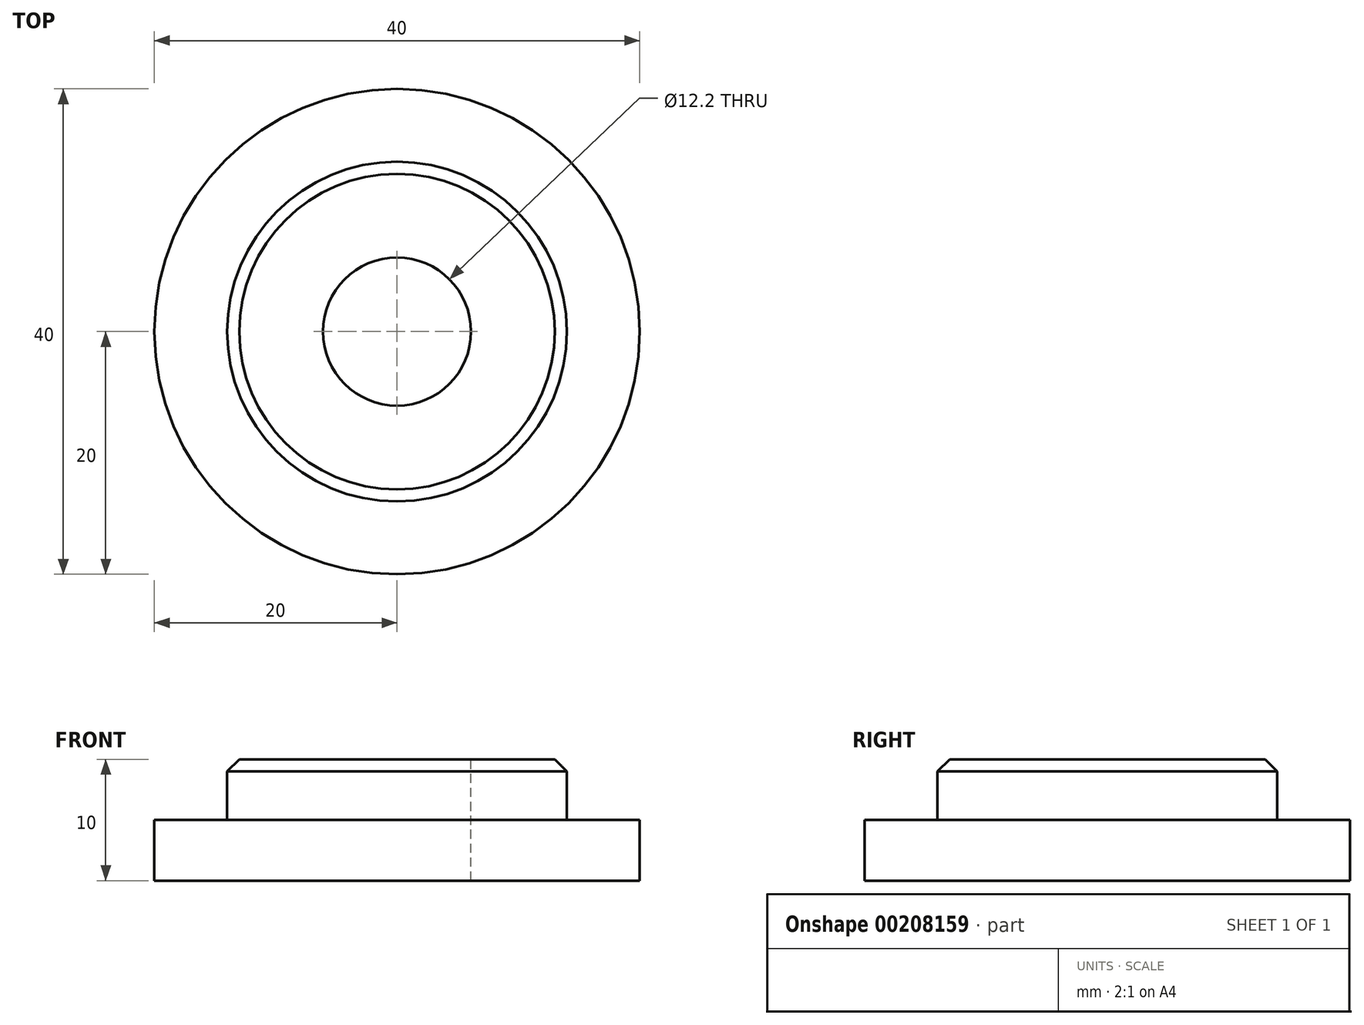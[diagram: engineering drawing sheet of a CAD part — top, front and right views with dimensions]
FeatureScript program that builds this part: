
annotation { "Feature Type Name" : "Feature", "Feature Type Description" : "" }
export const myFeature = defineFeature(function(context is Context, id is Id, definition is map)
    precondition{}
    {
        {
            var Q0;
            Q0=qCreatedBy(makeId("Top.planeOp"),FACE);
            var sketch = newSketch(context, id + "F0", { "sketchPlane" : qUnion([Q0])});
            skCircle(sketch, "E0", {"center": v(0, 0) * mm, "radius": 20 * mm});
            skSolve(sketch);
        }
        {
            var Q0;
            Q0=makeQuery(id+"F0.imprint","IMPRINT",FACE,{"disambiguationData":[TD([[makeQuery(id+"F0.imprint","IMPRINT",EDGE,{"derivedFrom":sQuery(id+"F0.wireOp",EDGE,"E0")}),1.0]])]});
            extrude(context, id + "F1", {"entities" : qUnion([Q0]), "depth" : 5 * mm});
        }
        {
            var Q0;
            Q0=makeQuery(id+"F1.opExtrude","CAP_FACE",FACE,{"disambiguationData":[OSD([sQuery(id+"F0.wireOp",EDGE,"E0")])],"isStart":false});
            var sketch = newSketch(context, id + "F2", { "sketchPlane" : qUnion([Q0])});
            skCircle(sketch, "E1", {"center": v(0, 0) * mm, "radius": 14 * mm});
            skSolve(sketch);
        }
        {
            var Q0;
            Q0=makeQuery(id+"F2.imprint","IMPRINT",FACE,{"disambiguationData":[TD([[makeQuery(id+"F2.imprint","IMPRINT",EDGE,{"derivedFrom":sQuery(id+"F2.wireOp",EDGE,"E1")}),1.0]])]});
            extrude(context, id + "F3", {"entities" : qUnion([Q0]), "operationType" : NewBodyOperationType.ADD, "depth" : 5 * mm});
        }
        {
            var Q0;
            Q0=makeQuery(id+"F1.opExtrude","CAP_FACE",FACE,{"disambiguationData":[OSD([sQuery(id+"F0.wireOp",EDGE,"E0")])],"isStart":true});
            var sketch = newSketch(context, id + "F4", { "sketchPlane" : qUnion([Q0])});
            skPoint(sketch, "E2", {"position": v(0, 0) * mm});
            skSolve(sketch);
        }
        {
            var Q0;
            Q0=sQuery(id+"F4.wireOp",VERTEX,"E2");
            var Q1;
            Q1=makeQuery(id+"F1.opExtrude","SWEPT_BODY",BODY,{"disambiguationData":[OSD([sQuery(id+"F0.wireOp",EDGE,"E0")])]});
            hole(context, id + "F5", {"style" : HoleStyle.SIMPLE, "endStyle" : HoleEndStyle.THROUGH, "holeDiameter" : 12.2 * mm, "locations" : qUnion([Q0]), "scope" : qUnion([Q1]), "isTappedThrough" : true, "startStyle" : HoleStartStyle.PART});
        }
        {
            var Q0;
            Q0=makeQuery(id+"F3.opExtrude","CAP_EDGE",EDGE,{"disambiguationData":[OSD([sQuery(id+"F2.wireOp",EDGE,"E1")])],"isStart":false});
            chamfer(context, id + "F6", {"entities" : qUnion([Q0]), "width" : 1 * mm, "tangentPropagation" : true});
        }
    });
